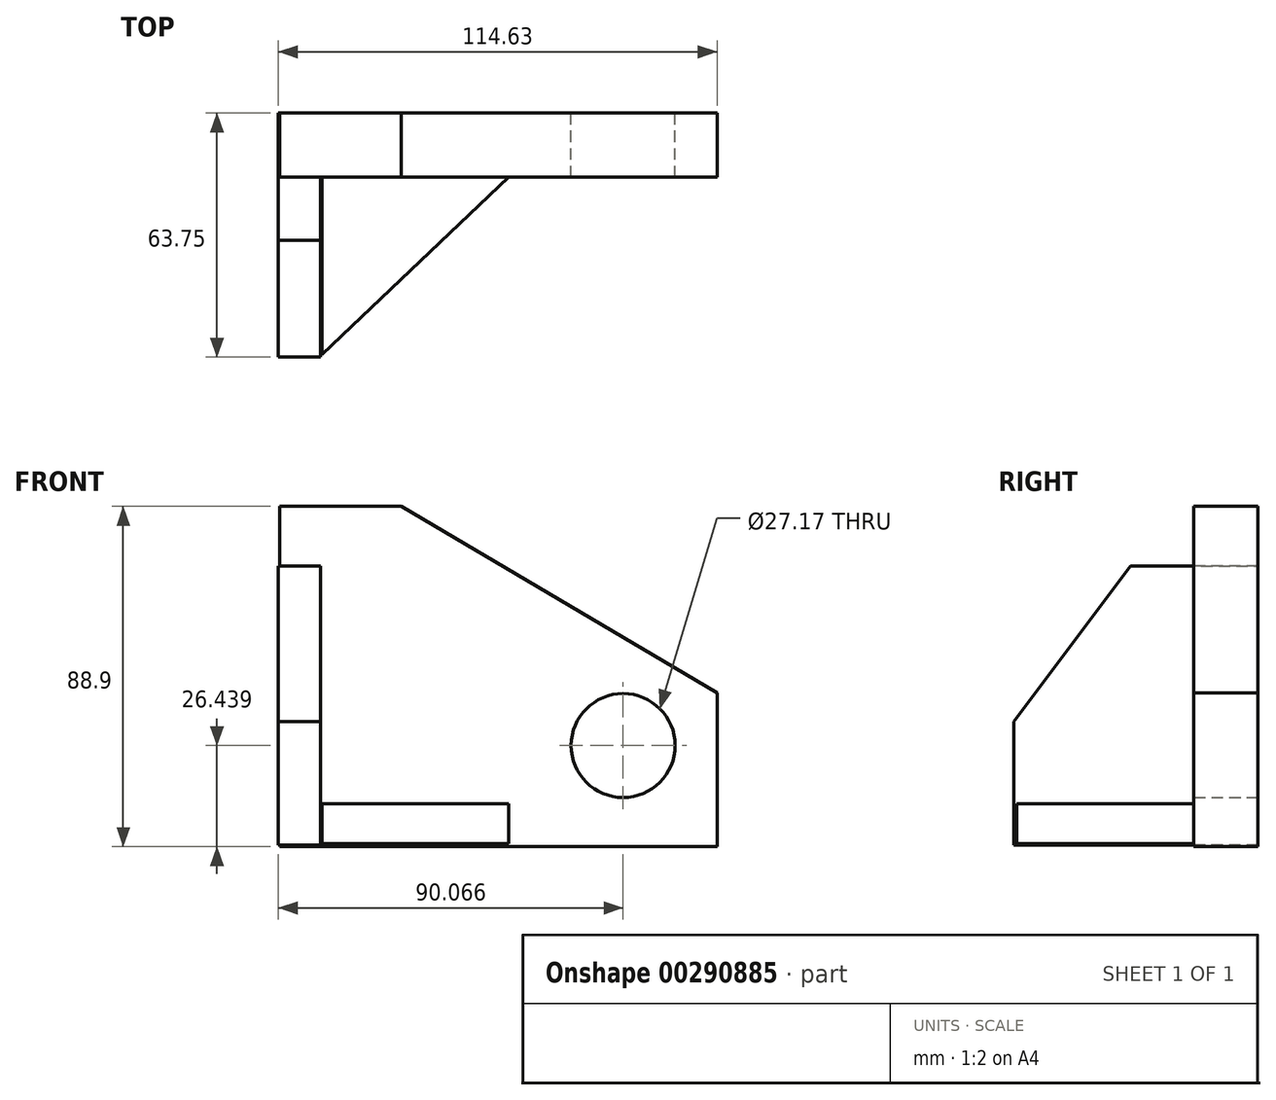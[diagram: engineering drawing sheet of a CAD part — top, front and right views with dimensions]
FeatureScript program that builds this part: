
annotation { "Feature Type Name" : "Feature", "Feature Type Description" : "" }
export const myFeature = defineFeature(function(context is Context, id is Id, definition is map)
    precondition{}
    {
        {
            var Q0;
            Q0=qCreatedBy(makeId("Front.planeOp"),FACE);
            var sketch = newSketch(context, id + "F0", { "sketchPlane" : qUnion([Q0])});
            skLineSegment(sketch, "E0", {"start": v(-60.88, 37.54) * mm, "end": v(-60.88, -51.36) * mm});
            skLineSegment(sketch, "E1", {"start": v(-60.88, 37.54) * mm, "end": v(-29.13, 37.54) * mm});
            skLineSegment(sketch, "E2", {"start": v(-60.88, -51.36) * mm, "end": v(53.42, -51.36) * mm});
            skLineSegment(sketch, "E3", {"start": v(53.42, -51.36) * mm, "end": v(53.42, -11.11) * mm});
            skLineSegment(sketch, "E4", {"start": v(53.42, -11.11) * mm, "end": v(-29.13, 37.54) * mm});
            skCircle(sketch, "E5", {"center": v(28.86, -24.92) * mm, "radius": 13.59 * mm});
            skSolve(sketch);
        }
        {
            var Q0;
            Q0 = qSketchRegion(id + "F0", true);
            extrude(context, id + "F1", {"entities" : qUnion([Q0]), "depth" : 16.76 * mm});
        }
        {
            var Q0;
            Q0=qCreatedBy(makeId("Front.planeOp"),FACE);
            var sketch = newSketch(context, id + "F2", { "sketchPlane" : qUnion([Q0])});
            skLineSegment(sketch, "E6.bottom", {"start": v(-61.2, 22) * mm, "end": v(-50.13, 22) * mm});
            skLineSegment(sketch, "E6.top", {"start": v(-61.2, -50.86) * mm, "end": v(-50.13, -50.86) * mm});
            skLineSegment(sketch, "E6.left", {"start": v(-61.2, 22) * mm, "end": v(-61.2, -50.86) * mm});
            skLineSegment(sketch, "E6.right", {"start": v(-50.13, 22) * mm, "end": v(-50.13, -50.86) * mm});
            skSolve(sketch);
        }
        {
            var Q0;
            Q0 = qSketchRegion(id + "F2", true);
            extrude(context, id + "F3", {"entities" : qUnion([Q0]), "operationType" : NewBodyOperationType.ADD, "depth" : 63.75 * mm});
        }
        {
            var Q0;
            Q0=makeQuery(id+"F3.opExtrude","CAP_EDGE",EDGE,{"disambiguationData":[OSD([sQuery(id+"F2.wireOp",EDGE,"E6.bottom")])],"isStart":false});
            chamfer(context, id + "F4", {"entities" : qUnion([Q0]), "chamferType" : ChamferType.TWO_OFFSETS, "width1" : 30.48 * mm, "oppositeDirection" : false, "width2" : 40.64 * mm, "tangentPropagation" : true});
        }
        {
            var Q0;
            Q0=qCreatedBy(makeId("Front.planeOp"),FACE);
            var sketch = newSketch(context, id + "F5", { "sketchPlane" : qUnion([Q0])});
            skLineSegment(sketch, "E7.bottom", {"start": v(-49.84, -40.08) * mm, "end": v(0, -40.08) * mm});
            skLineSegment(sketch, "E7.top", {"start": v(-49.84, -50.57) * mm, "end": v(0, -50.57) * mm});
            skLineSegment(sketch, "E7.left", {"start": v(-49.84, -40.08) * mm, "end": v(-49.84, -50.57) * mm});
            skLineSegment(sketch, "E7.right", {"start": v(0, -40.08) * mm, "end": v(0, -50.57) * mm});
            skSolve(sketch);
        }
        {
            var Q0;
            Q0 = qSketchRegion(id + "F5", true);
            extrude(context, id + "F6", {"entities" : qUnion([Q0]), "operationType" : NewBodyOperationType.ADD, "depth" : 64 * mm});
        }
        {
            var Q0;
            Q0=makeQuery(id+"F6.opExtrude","CAP_EDGE",EDGE,{"disambiguationData":[OSD([sQuery(id+"F5.wireOp",EDGE,"E7.right")])],"isStart":false});
            chamfer(context, id + "F7", {"entities" : qUnion([Q0]), "chamferType" : ChamferType.TWO_OFFSETS, "width1" : 48.26 * mm, "oppositeDirection" : false, "width2" : 50.8 * mm, "tangentPropagation" : true});
        }
    });
